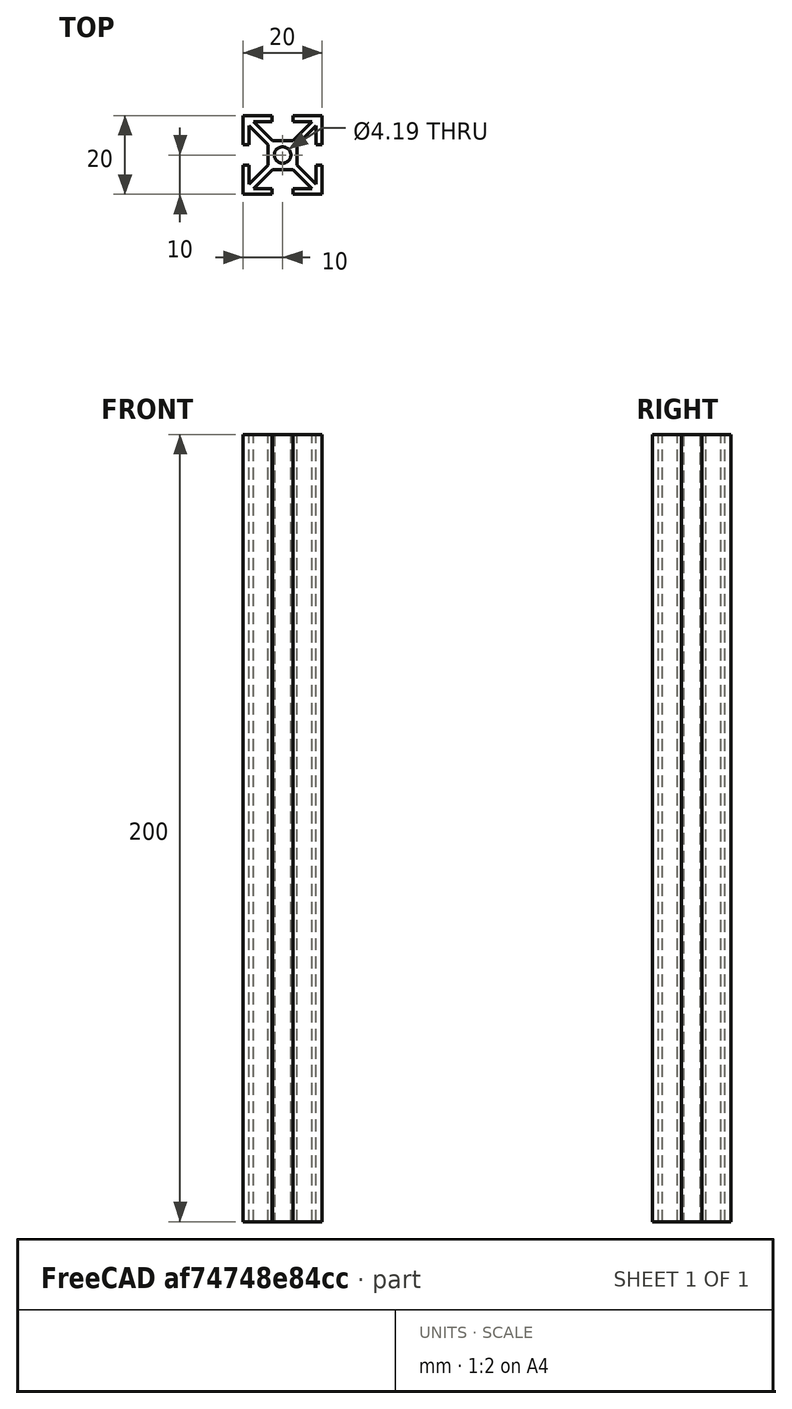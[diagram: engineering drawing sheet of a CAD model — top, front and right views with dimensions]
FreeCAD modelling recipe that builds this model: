
FCSTD DOCUMENT  (FreeCAD 0.15R4671 (Git))
Label: 20series-1x1_20mm
License: All rights reserved
LicenseURL: http://en.wikipedia.org/wiki/All_rights_reserved
objects: Sketcher::SketchObject×1, Part::Extrusion×1
note: 2 computed .brp shape members not serialized (recipe doc carries the construction recipe); baked Part::Feature solids carry a one-line shape summary decoded from their .brp

FEATURE [Sketcher::SketchObject] Sketch  label="20seriesProfile"
  sketch-geometry (93):
    g0: LineSegment [constr] StartX=0 StartY=0 StartZ=0 EndX=20 EndY=0 EndZ=0
    g1: LineSegment [constr] StartX=20 StartY=0 StartZ=0 EndX=20 EndY=20 EndZ=0
    g2: LineSegment [constr] StartX=20 StartY=20 StartZ=0 EndX=0 EndY=20 EndZ=0
    g3: LineSegment [constr] StartX=0 StartY=20 StartZ=0 EndX=0 EndY=0 EndZ=0
    g4: LineSegment [constr] StartX=0 StartY=0 StartZ=0 EndX=20 EndY=20 EndZ=0
    g5: LineSegment [constr] StartX=0 StartY=20 StartZ=0 EndX=20 EndY=0 EndZ=0
    g6: GeomPoint [constr] X=0 Y=10 Z=0
    g7: GeomPoint [constr] X=20 Y=10 Z=0
    g8: GeomPoint [constr] X=10 Y=20 Z=0
    g9: GeomPoint [constr] X=10 Y=0 Z=0
    g10: LineSegment [constr] StartX=0 StartY=10 StartZ=0 EndX=20 EndY=10 EndZ=0
    g11: LineSegment [constr] StartX=10 StartY=20 StartZ=0 EndX=10 EndY=0 EndZ=0
    g12: GeomPoint [constr] X=10 Y=10 Z=0
    g13: Circle CenterX=10 CenterY=10 CenterZ=0 NormalX=0 NormalY=0 NormalZ=1 Radius=2.095
    g14: LineSegment StartX=6.34 StartY=6.34 StartZ=0 EndX=13.66 EndY=6.34 EndZ=0
    g15: LineSegment StartX=13.66 StartY=6.34 StartZ=0 EndX=13.66 EndY=13.66 EndZ=0
    g16: LineSegment StartX=13.66 StartY=13.66 StartZ=0 EndX=6.34 EndY=13.66 EndZ=0
    g17: LineSegment StartX=6.34 StartY=13.66 StartZ=0 EndX=6.34 EndY=6.34 EndZ=0
    g18: LineSegment [constr] StartX=1.5 StartY=1.5 StartZ=0 EndX=18.5 EndY=1.5 EndZ=0
    g19: LineSegment [constr] StartX=18.5 StartY=1.5 StartZ=0 EndX=18.5 EndY=18.5 EndZ=0
    g20: LineSegment [constr] StartX=18.5 StartY=18.5 StartZ=0 EndX=1.5 EndY=18.5 EndZ=0
    g21: LineSegment [constr] StartX=1.5 StartY=18.5 StartZ=0 EndX=1.5 EndY=1.5 EndZ=0
    g22: LineSegment [constr] StartX=1.5 StartY=1.5 StartZ=0 EndX=0 EndY=1.5 EndZ=0
    g23: LineSegment [constr] StartX=2.56066 StartY=1.5 StartZ=0 EndX=7.40066 EndY=6.34 EndZ=0
    g24: LineSegment [constr] StartX=6.34 StartY=7.40066 StartZ=0 EndX=1.5 EndY=2.56066 EndZ=0
    g25: LineSegment [constr] StartX=1.5 StartY=2.56066 StartZ=0 EndX=2.56066 EndY=1.5 EndZ=0
    g26: LineSegment [constr] StartX=17.4393 StartY=1.5 StartZ=0 EndX=12.5993 EndY=6.34 EndZ=0
    g27: LineSegment [constr] StartX=13.66 StartY=7.40066 StartZ=0 EndX=18.5 EndY=2.56066 EndZ=0
    g28: LineSegment [constr] StartX=2.56066 StartY=18.5 StartZ=0 EndX=7.40066 EndY=13.66 EndZ=0
    g29: LineSegment [constr] StartX=1.5 StartY=17.4393 StartZ=0 EndX=6.34 EndY=12.5993 EndZ=0
    g30: LineSegment [constr] StartX=2.56066 StartY=18.5 StartZ=0 EndX=1.5 EndY=17.4393 EndZ=0
    g31: LineSegment [constr] StartX=18.5 StartY=2.56066 StartZ=0 EndX=17.4393 EndY=1.5 EndZ=0
    g32: LineSegment [constr] StartX=17.4393 StartY=18.5 StartZ=0 EndX=12.5993 EndY=13.66 EndZ=0
    g33: LineSegment [constr] StartX=13.66 StartY=12.5993 StartZ=0 EndX=18.5 EndY=17.4393 EndZ=0
    g34: LineSegment [constr] StartX=18.5 StartY=17.4393 StartZ=0 EndX=17.4393 EndY=18.5 EndZ=0
    g35: LineSegment [constr] StartX=0 StartY=7.37 StartZ=0 EndX=1.5 EndY=7.37 EndZ=0
    g36: LineSegment [constr] StartX=1.5 StartY=12.63 StartZ=0 EndX=0 EndY=12.63 EndZ=0
    g37: LineSegment [constr] StartX=0.75 StartY=12.63 StartZ=0 EndX=0.75 EndY=7.37 EndZ=0
    g38: GeomPoint [constr] X=0.75 Y=10 Z=0
    g39: LineSegment [constr] StartX=18.5 StartY=12.63 StartZ=0 EndX=20 EndY=12.63 EndZ=0
    g40: LineSegment [constr] StartX=18.5 StartY=7.37 StartZ=0 EndX=20 EndY=7.37 EndZ=0
    g41: LineSegment [constr] StartX=7.37 StartY=1.5 StartZ=0 EndX=7.37 EndY=0 EndZ=0
    g42: LineSegment [constr] StartX=12.63 StartY=1.5 StartZ=0 EndX=12.63 EndY=0 EndZ=0
    g43: LineSegment [constr] StartX=7.37 StartY=0.75 StartZ=0 EndX=12.63 EndY=0.75 EndZ=0
    g44: LineSegment [constr] StartX=7.37 StartY=20 StartZ=0 EndX=7.37 EndY=18.5 EndZ=0
    g45: LineSegment [constr] StartX=12.63 StartY=20 StartZ=0 EndX=12.63 EndY=18.5 EndZ=0
    g46: GeomPoint [constr] X=7.37 Y=19.25 Z=0
    g47: LineSegment [constr] StartX=7.37 StartY=19.25 StartZ=0 EndX=12.63 EndY=19.25 EndZ=0
    g48: GeomPoint [constr] X=19.25 Y=12.63 Z=0
    g49: LineSegment [constr] StartX=19.25 StartY=12.63 StartZ=0 EndX=19.25 EndY=7.37 EndZ=0
    g50: GeomPoint [constr] X=19.25 Y=10 Z=0
    g51: GeomPoint [constr] X=10 Y=19.25 Z=0
    g52: GeomPoint [constr] X=10 Y=0.75 Z=0
    g53: LineSegment StartX=0 StartY=7.37 StartZ=0 EndX=0 EndY=0 EndZ=0
    g54: LineSegment StartX=0 StartY=0 StartZ=0 EndX=7.37 EndY=0 EndZ=0
    g55: LineSegment StartX=7.37 StartY=0 StartZ=0 EndX=7.37 EndY=1.5 EndZ=0
    g56: LineSegment StartX=7.37 StartY=1.5 StartZ=0 EndX=2.56066 EndY=1.5 EndZ=0
    g57: LineSegment StartX=2.56066 StartY=1.5 StartZ=0 EndX=7.40066 EndY=6.34 EndZ=0
    g58: LineSegment StartX=7.40066 StartY=6.34 StartZ=0 EndX=6.34 EndY=6.34 EndZ=0
    g59: LineSegment StartX=6.34 StartY=6.34 StartZ=0 EndX=6.34 EndY=7.40066 EndZ=0
    g60: LineSegment StartX=6.34 StartY=7.40066 StartZ=0 EndX=1.5 EndY=2.56066 EndZ=0
    g61: LineSegment StartX=1.5 StartY=2.56066 StartZ=0 EndX=1.5 EndY=7.37 EndZ=0
    g62: LineSegment StartX=1.5 StartY=7.37 StartZ=0 EndX=0 EndY=7.37 EndZ=0
    g63: LineSegment StartX=20 StartY=7.37 StartZ=0 EndX=20 EndY=0 EndZ=0
    g64: LineSegment StartX=20 StartY=0 StartZ=0 EndX=12.63 EndY=0 EndZ=0
    g65: LineSegment StartX=12.63 StartY=0 StartZ=0 EndX=12.63 EndY=1.5 EndZ=0
    g66: LineSegment StartX=12.63 StartY=1.5 StartZ=0 EndX=17.4393 EndY=1.5 EndZ=0
    g67: LineSegment StartX=17.4393 StartY=1.5 StartZ=0 EndX=12.5993 EndY=6.34 EndZ=0
    g68: LineSegment StartX=12.5993 StartY=6.34 StartZ=0 EndX=13.66 EndY=6.34 EndZ=0
    g69: LineSegment StartX=13.66 StartY=6.34 StartZ=0 EndX=13.66 EndY=7.40066 EndZ=0
    g70: LineSegment StartX=13.66 StartY=7.40066 StartZ=0 EndX=18.5 EndY=2.56066 EndZ=0
    g71: LineSegment StartX=18.5 StartY=2.56066 StartZ=0 EndX=18.5 EndY=7.37 EndZ=0
    g72: LineSegment StartX=18.5 StartY=7.37 StartZ=0 EndX=20 EndY=7.37 EndZ=0
    g73: LineSegment StartX=1.5 StartY=12.63 StartZ=0 EndX=1.5 EndY=17.4393 EndZ=0
    g74: LineSegment StartX=1.5 StartY=17.4393 StartZ=0 EndX=6.34 EndY=12.5993 EndZ=0
    g75: LineSegment StartX=6.34 StartY=12.5993 StartZ=0 EndX=6.34 EndY=13.66 EndZ=0
    g76: LineSegment StartX=6.34 StartY=13.66 StartZ=0 EndX=7.40066 EndY=13.66 EndZ=0
    g77: LineSegment StartX=7.40066 StartY=13.66 StartZ=0 EndX=2.56066 EndY=18.5 EndZ=0
    g78: LineSegment StartX=2.56066 StartY=18.5 StartZ=0 EndX=7.37 EndY=18.5 EndZ=0
    g79: LineSegment StartX=7.37 StartY=18.5 StartZ=0 EndX=7.37 EndY=20 EndZ=0
    g80: LineSegment StartX=7.37 StartY=20 StartZ=0 EndX=0 EndY=20 EndZ=0
    g81: LineSegment StartX=0 StartY=20 StartZ=0 EndX=0 EndY=12.63 EndZ=0
    g82: LineSegment StartX=0 StartY=12.63 StartZ=0 EndX=1.5 EndY=12.63 EndZ=0
    g83: LineSegment StartX=20 StartY=12.63 StartZ=0 EndX=20 EndY=20 EndZ=0
    g84: LineSegment StartX=20 StartY=20 StartZ=0 EndX=12.63 EndY=20 EndZ=0
    g85: LineSegment StartX=12.63 StartY=20 StartZ=0 EndX=12.63 EndY=18.5 EndZ=0
    g86: LineSegment StartX=12.63 StartY=18.5 StartZ=0 EndX=17.4393 EndY=18.5 EndZ=0
    g87: LineSegment StartX=17.4393 StartY=18.5 StartZ=0 EndX=12.5993 EndY=13.66 EndZ=0
    g88: LineSegment StartX=12.5993 StartY=13.66 StartZ=0 EndX=13.66 EndY=13.66 EndZ=0
    g89: LineSegment StartX=13.66 StartY=13.66 StartZ=0 EndX=13.66 EndY=12.5993 EndZ=0
    g90: LineSegment StartX=13.66 StartY=12.5993 StartZ=0 EndX=18.5 EndY=17.4393 EndZ=0
    g91: LineSegment StartX=18.5 StartY=17.4393 StartZ=0 EndX=18.5 EndY=12.63 EndZ=0
    g92: LineSegment StartX=18.5 StartY=12.63 StartZ=0 EndX=20 EndY=12.63 EndZ=0
  constraints (233):
    c: Coincident(g0,g1)
    c: Coincident(g1,g2)
    c: Coincident(g2,g3)
    c: Coincident(g3,g0)
    c: Horizontal(g0)
    c: Vertical(g1)
    c: Coincident(g0,g-1)
    c: Equal(g0,g3)
    c: DistanceX(g0) = 20
    c: Coincident(g4,g-1)
    c: Coincident(g4,g1)
    c: Coincident(g5,g2)
    c: Coincident(g5,g0)
    c: PointOnObject(g8,g2)
    c: Symmetric(g0,g0,g9)
    c: Symmetric(g1,g1,g7)
    c: Symmetric(g2,g2,g8)
    c: Symmetric(g3,g3,g6)
    c: Horizontal(g10)
    c: Coincident(g10,g7)
    c: Coincident(g10,g6)
    c: PointOnObject(g11,g2)
    c: PointOnObject(g11,g0)
    c: Vertical(g11)
    c: Coincident(g11,g9)
    c: PointOnObject(g12,g11)
    c: Symmetric(g10,g10,g12)
    c: Radius(g13) = 2.095
    c: Coincident(g13,g12)
    c: Coincident(g14,g15)
    c: Coincident(g15,g16)
    c: Coincident(g16,g17)
    c: Coincident(g17,g14)
    c: Horizontal(g14)
    c: Horizontal(g16)
    c: Vertical(g15)
    c: Vertical(g17)
    c: PointOnObject(g14,g4)
    c: PointOnObject(g15,g4)
    c: PointOnObject(g14,g5)
    c: DistanceX(g14) = 7.32
    c: Coincident(g18,g19)
    c: Coincident(g19,g20)
    c: Coincident(g20,g21)
    c: Coincident(g21,g18)
    c: Horizontal(g18)
    c: Vertical(g21)
    c: PointOnObject(g18,g4)
    c: PointOnObject(g19,g4)
    c: Equal(g21,g18)
    c: PointOnObject(g20,g5)
    c: Coincident(g22,g18)
    c: PointOnObject(g22,g3)
    c: Horizontal(g22)
    c: DistanceX(g22) = -1.5
    c: PointOnObject(g23,g14)
    c: Parallel(g23,g4)
    c: PointOnObject(g24,g17)
    c: PointOnObject(g24,g21)
    c: Parallel(g24,g4)
    c: PointOnObject(g23,g18)
    c: Coincident(g25,g24)
    c: Coincident(g25,g23)
    c: Perpendicular(g4,g25)
    c: Distance(g25) = 1.5
    c: PointOnObject(g26,g18)
    c: PointOnObject(g26,g14)
    c: PointOnObject(g27,g15)
    c: PointOnObject(g27,g19)
    c: PointOnObject(g28,g20)
    c: PointOnObject(g28,g16)
    c: PointOnObject(g29,g21)
    c: PointOnObject(g29,g17)
    c: Parallel(g29,g28)
    c: Parallel(g28,g27)
    c: Parallel(g27,g26)
    c: Parallel(g26,g5)
    c: Coincident(g30,g28)
    c: Coincident(g29,g30)
    c: Coincident(g31,g27)
    c: Coincident(g31,g26)
    c: Perpendicular(g5,g31)
    c: Perpendicular(g5,g30)
    c: Equal(g31,g30)
    c: Equal(g30,g25)
    c: PointOnObject(g32,g20)
    c: PointOnObject(g32,g16)
    c: PointOnObject(g33,g15)
    c: PointOnObject(g33,g19)
    c: Coincident(g34,g33)
    c: Parallel(g33,g32)
    c: Parallel(g32,g4)
    c: Coincident(g34,g32)
    c: Perpendicular(g4,g34)
    c: Equal(g34,g25)
    c: PointOnObject(g35,g3)
    c: PointOnObject(g35,g21)
    c: Horizontal(g35)
    c: PointOnObject(g36,g21)
    c: Horizontal(g36)
    c: Vertical(g37)
    c: Symmetric(g37,g37,g38)
    c: PointOnObject(g38,g10)
    c: PointOnObject(g37,g36)
    c: PointOnObject(g37,g35)
    c: Symmetric(g36,g36,g37)
    c: PointOnObject(g36,g3)
    c: DistanceY(g36,g35) = -5.26
    c: PointOnObject(g39,g19)
    c: PointOnObject(g39,g1)
    c: Horizontal(g39)
    c: PointOnObject(g40,g19)
    c: PointOnObject(g40,g1)
    c: Horizontal(g40)
    c: PointOnObject(g41,g18)
    c: PointOnObject(g41,g0)
    c: Vertical(g41)
    c: PointOnObject(g42,g18)
    c: PointOnObject(g42,g0)
    c: Vertical(g42)
    c: PointOnObject(g43,g41)
    c: PointOnObject(g43,g42)
    c: Horizontal(g43)
    c: Symmetric(g41,g41,g43)
    c: PointOnObject(g44,g2)
    c: PointOnObject(g44,g20)
    c: Vertical(g44)
    c: Vertical(g45)
    c: PointOnObject(g46,g44)
    c: Coincident(g47,g46)
    c: PointOnObject(g47,g45)
    c: Horizontal(g47)
    c: Symmetric(g44,g44,g46)
    c: PointOnObject(g48,g39)
    c: Coincident(g49,g48)
    c: PointOnObject(g49,g40)
    c: Vertical(g49)
    c: Symmetric(g39,g39,g48)
    c: PointOnObject(g50,g49)
    c: PointOnObject(g50,g10)
    c: PointOnObject(g51,g47)
    c: Symmetric(g47,g47,g51)
    c: PointOnObject(g51,g11)
    c: Equal(g47,g49)
    c: Equal(g49,g43)
    c: PointOnObject(g52,g43)
    c: Symmetric(g43,g43,g52)
    c: PointOnObject(g52,g11)
    c: Equal(g37,g47)
    c: Symmetric(g49,g49,g50)
    c: PointOnObject(g45,g2)
    c: PointOnObject(g45,g20)
    c: Coincident(g35,g53)
    c: Coincident(g53,g-1)
    c: Coincident(g53,g54)
    c: Coincident(g54,g41)
    c: Coincident(g54,g55)
    c: Coincident(g55,g41)
    c: Coincident(g55,g56)
    c: Coincident(g56,g23)
    c: Coincident(g56,g57)
    c: Coincident(g57,g23)
    c: Coincident(g57,g58)
    c: Coincident(g58,g14)
    c: Coincident(g58,g59)
    c: Coincident(g59,g24)
    c: Coincident(g59,g60)
    c: Coincident(g60,g24)
    c: Coincident(g60,g61)
    c: Coincident(g61,g35)
    c: Coincident(g61,g62)
    c: Coincident(g62,g53)
    c: Coincident(g40,g63)
    c: Coincident(g63,g0)
    c: Coincident(g63,g64)
    c: Coincident(g64,g42)
    c: Coincident(g64,g65)
    c: Coincident(g65,g42)
    c: Coincident(g65,g66)
    c: Coincident(g66,g26)
    c: Coincident(g66,g67)
    c: Coincident(g67,g26)
    c: Coincident(g67,g68)
    c: Coincident(g68,g14)
    c: Coincident(g68,g69)
    c: Coincident(g69,g27)
    c: Coincident(g69,g70)
    c: Coincident(g70,g27)
    c: Coincident(g70,g71)
    c: Coincident(g71,g40)
    c: Coincident(g71,g72)
    c: Coincident(g72,g63)
    c: Coincident(g36,g73)
    c: Coincident(g73,g29)
    c: Coincident(g73,g74)
    c: Coincident(g74,g29)
    c: Coincident(g74,g75)
    c: Coincident(g75,g16)
    c: Coincident(g75,g76)
    c: Coincident(g76,g28)
    c: Coincident(g76,g77)
    c: Coincident(g77,g28)
    c: Coincident(g77,g78)
    c: Coincident(g78,g44)
    c: Coincident(g78,g79)
    c: Coincident(g79,g44)
    c: Coincident(g79,g80)
    c: Coincident(g80,g2)
    c: Coincident(g80,g81)
    c: Coincident(g81,g36)
    c: Coincident(g81,g82)
    c: Coincident(g82,g73)
    c: Coincident(g39,g83)
    c: Coincident(g83,g1)
    c: Coincident(g83,g84)
    c: Coincident(g84,g45)
    c: Coincident(g84,g85)
    c: Coincident(g85,g45)
    c: Coincident(g85,g86)
    c: Coincident(g86,g32)
    c: Horizontal(g86)
    c: Coincident(g86,g87)
    c: Coincident(g87,g32)
    c: Coincident(g87,g88)
    c: Coincident(g88,g15)
    c: Coincident(g88,g89)
    c: Coincident(g89,g90)
    c: Coincident(g90,g33)
    c: Coincident(g90,g91)
    c: Coincident(g91,g39)
    c: Coincident(g91,g92)
    c: Coincident(g92,g83)
    c: Coincident(g89,g33)
FEATURE [Part::Extrusion] Extrude
  Base = -> Sketch
  Dir = (0,0,200)
  Solid = true
